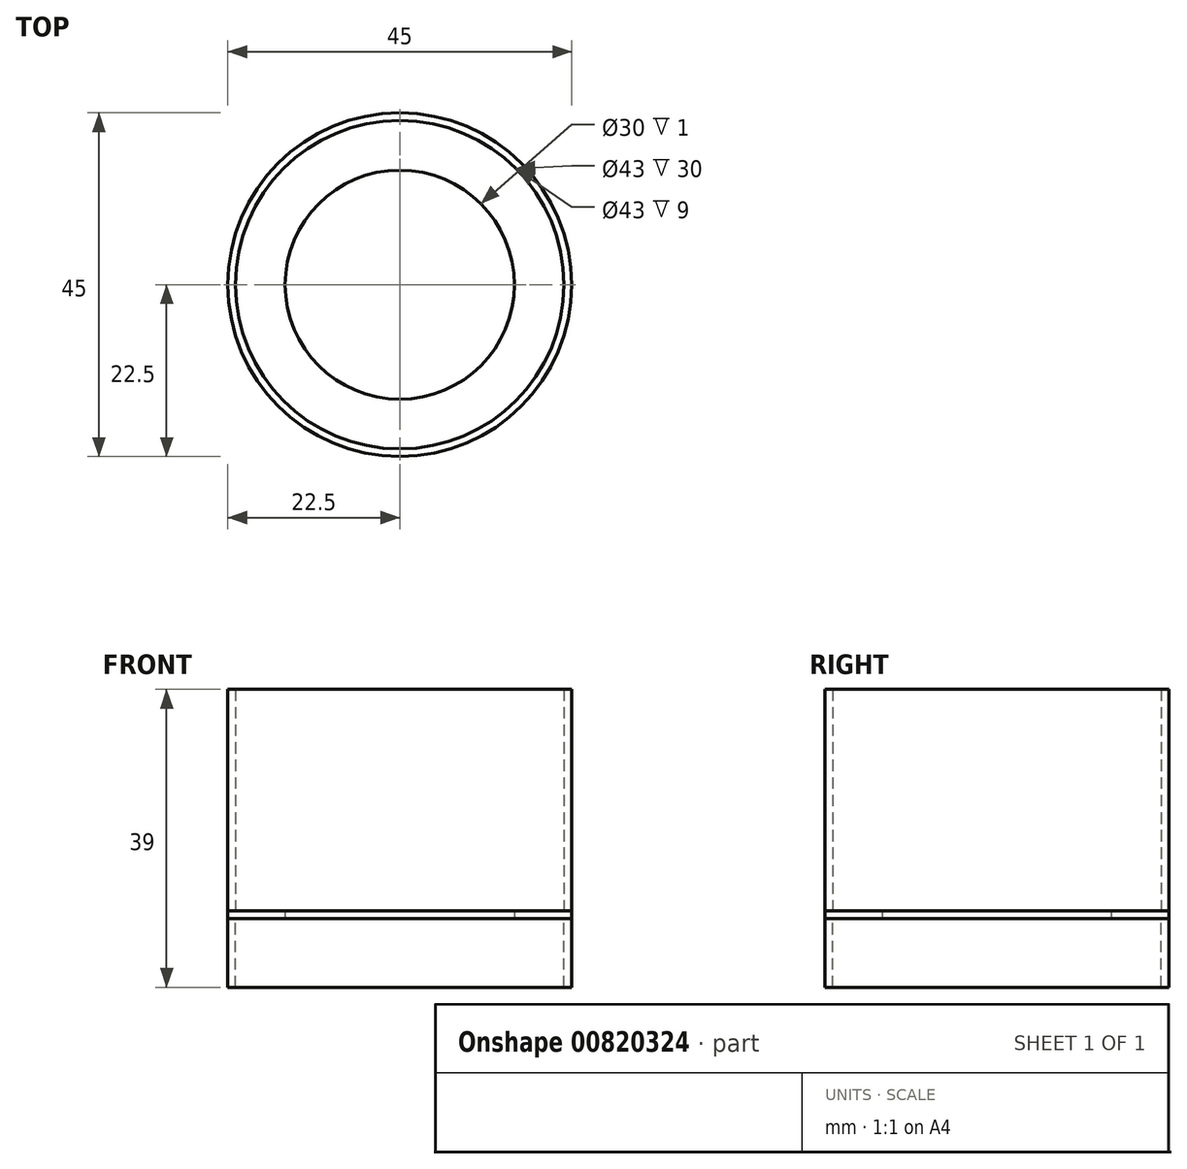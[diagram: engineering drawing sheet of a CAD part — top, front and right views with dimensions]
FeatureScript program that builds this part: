
annotation { "Feature Type Name" : "Feature", "Feature Type Description" : "" }
export const myFeature = defineFeature(function(context is Context, id is Id, definition is map)
    precondition{}
    {
        {
            var Q0;
            Q0=qCreatedBy(makeId("Top.planeOp"),FACE);
            var sketch = newSketch(context, id + "F0", { "sketchPlane" : qUnion([Q0])});
            skCircle(sketch, "E0", {"center": v(0, 0) * mm, "radius": 21.5 * mm});
            skCircle(sketch, "E1", {"center": v(0, 0) * mm, "radius": 22.5 * mm});
            skCircle(sketch, "E2", {"center": v(0, 0) * mm, "radius": 15 * mm});
            skSolve(sketch);
        }
        {
            var Q0;
            Q0 = qSketchRegion(id + "F0", true);
            extrude(context, id + "F1", {"entities" : qUnion([Q0]), "oppositeDirection" : true, "depth" : 9 * mm, "offsetDistance" : 25 * mm});
        }
        {
            var Q0;
            Q0=makeQuery(id+"F0.imprint","IMPRINT",FACE,{"disambiguationData":[TD([[makeQuery(id+"F0.imprint","IMPRINT",EDGE,{"derivedFrom":sQuery(id+"F0.wireOp",EDGE,"E0")}),1.0]])]});
            var Q1;
            Q1=makeQuery(id+"F0.imprint","IMPRINT",FACE,{"disambiguationData":[TD([[makeQuery(id+"F0.imprint","IMPRINT",EDGE,{"derivedFrom":sQuery(id+"F0.wireOp",EDGE,"E0")}),-1.0]])]});
            extrude(context, id + "F2", {"entities" : qUnion([Q0, Q1]), "depth" : 1 * mm, "offsetDistance" : 25 * mm});
        }
        {
            var Q0;
            Q0 = qSketchRegion(id + "F0", true);
            extrude(context, id + "F3", {"entities" : qUnion([Q0]), "depth" : 30 * mm, "offsetDistance" : 25 * mm});
        }
    });
